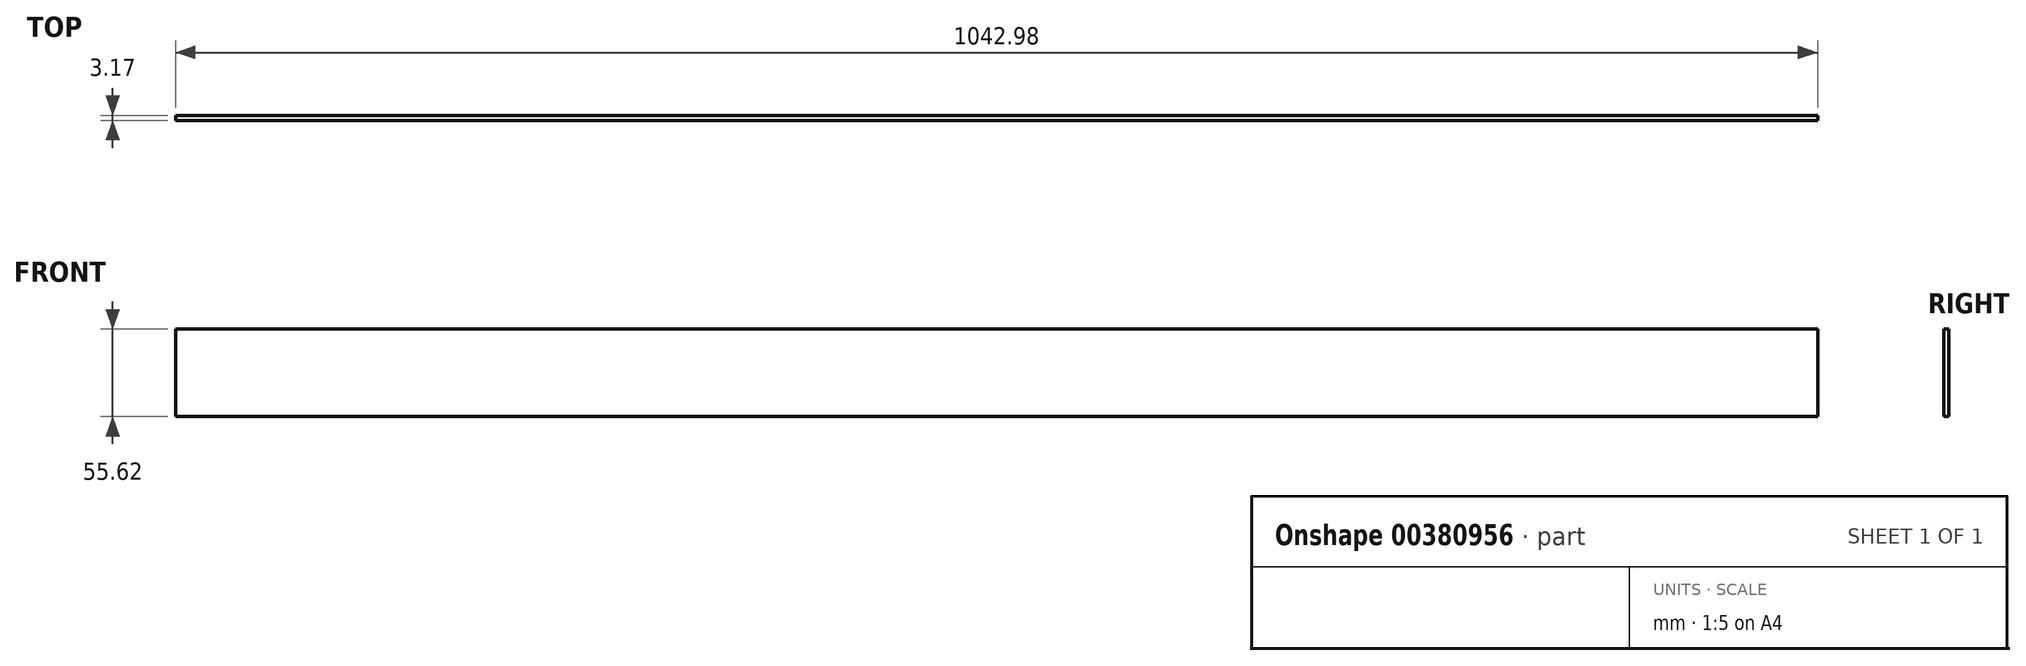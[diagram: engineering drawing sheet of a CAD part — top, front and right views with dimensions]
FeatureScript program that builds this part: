
annotation { "Feature Type Name" : "Feature", "Feature Type Description" : "" }
export const myFeature = defineFeature(function(context is Context, id is Id, definition is map)
    precondition{}
    {
        {
            var Q0;
            Q0=qCreatedBy(makeId("Front.planeOp"),FACE);
            var sketch = newSketch(context, id + "F0", { "sketchPlane" : qUnion([Q0])});
            skLineSegment(sketch, "E0.bottom", {"start": v(521.5, 27.81) * mm, "end": v(-521.5, 27.81) * mm});
            skLineSegment(sketch, "E0.top", {"start": v(521.5, -27.81) * mm, "end": v(-521.5, -27.81) * mm});
            skLineSegment(sketch, "E0.left", {"start": v(521.5, 27.81) * mm, "end": v(521.5, -27.81) * mm});
            skLineSegment(sketch, "E0.right", {"start": v(-521.5, 27.81) * mm, "end": v(-521.5, -27.81) * mm});
            skPoint(sketch, "E0.middle", {"position": v(0, 0) * mm});
            skSolve(sketch);
        }
        {
            var Q0;
            Q0=qSketchRegion(id+"F0",true);
            extrude(context, id + "F1", {"entities" : qUnion([Q0]), "depth" : 3.17 * mm});
        }
    });
